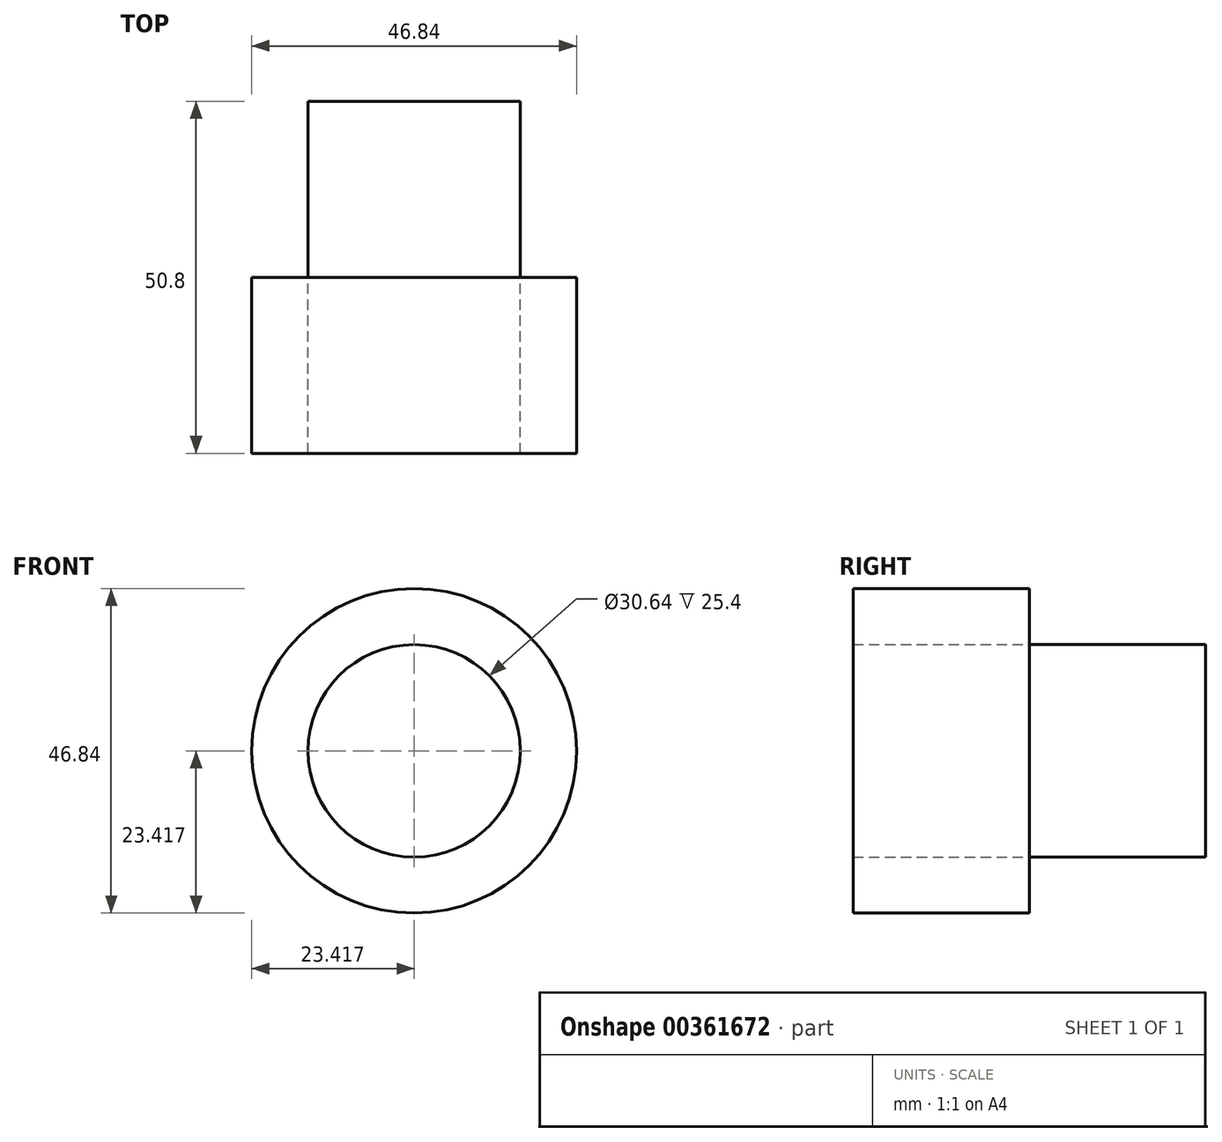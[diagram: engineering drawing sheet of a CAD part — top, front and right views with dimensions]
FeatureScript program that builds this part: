
annotation { "Feature Type Name" : "Feature", "Feature Type Description" : "" }
export const myFeature = defineFeature(function(context is Context, id is Id, definition is map)
    precondition{}
    {
        {
            var Q0;
            Q0=qCreatedBy(makeId("Front.planeOp"),FACE);
            var sketch = newSketch(context, id + "F0", { "sketchPlane" : qUnion([Q0])});
            skLineSegment(sketch, "E0", {"start": v(-62.83, 24.6) * mm, "end": v(-18.26, 35.75) * mm});
            skCircle(sketch, "E1", {"center": v(21.05, 43.49) * mm, "radius": 23.42 * mm});
            skCircle(sketch, "E2", {"center": v(21.05, 43.49) * mm, "radius": 15.32 * mm});
            skCircle(sketch, "E3", {"center": v(21.05, 43.49) * mm, "radius": 9.37 * mm});
            skSolve(sketch);
        }
        {
            var Q0;
            Q0=makeQuery(id+"F0.imprint","IMPRINT",FACE,{"disambiguationData":[TD([[makeQuery(id+"F0.imprint","IMPRINT",EDGE,{"derivedFrom":sQuery(id+"F0.wireOp",EDGE,"E1")}),1.0]])]});
            extrude(context, id + "F1", {"entities" : qUnion([Q0]), "depth" : 25.4 * mm});
        }
        {
            var Q0;
            Q0=makeQuery(id+"F0.imprint","IMPRINT",FACE,{"disambiguationData":[TD([[makeQuery(id+"F0.imprint","IMPRINT",EDGE,{"derivedFrom":sQuery(id+"F0.wireOp",EDGE,"E2")}),1.0]])]});
            extrude(context, id + "F2", {"entities" : qUnion([Q0]), "operationType" : NewBodyOperationType.ADD, "oppositeDirection" : true, "depth" : 25.4 * mm});
        }
        {
            var Q0;
            Q0=makeQuery(id+"F0.imprint","IMPRINT",FACE,{"disambiguationData":[TD([[makeQuery(id+"F0.imprint","IMPRINT",EDGE,{"derivedFrom":sQuery(id+"F0.wireOp",EDGE,"E3")}),1.0]])]});
            extrude(context, id + "F3", {"entities" : qUnion([Q0]), "operationType" : NewBodyOperationType.ADD, "oppositeDirection" : true, "depth" : 25.4 * mm});
        }
    });
